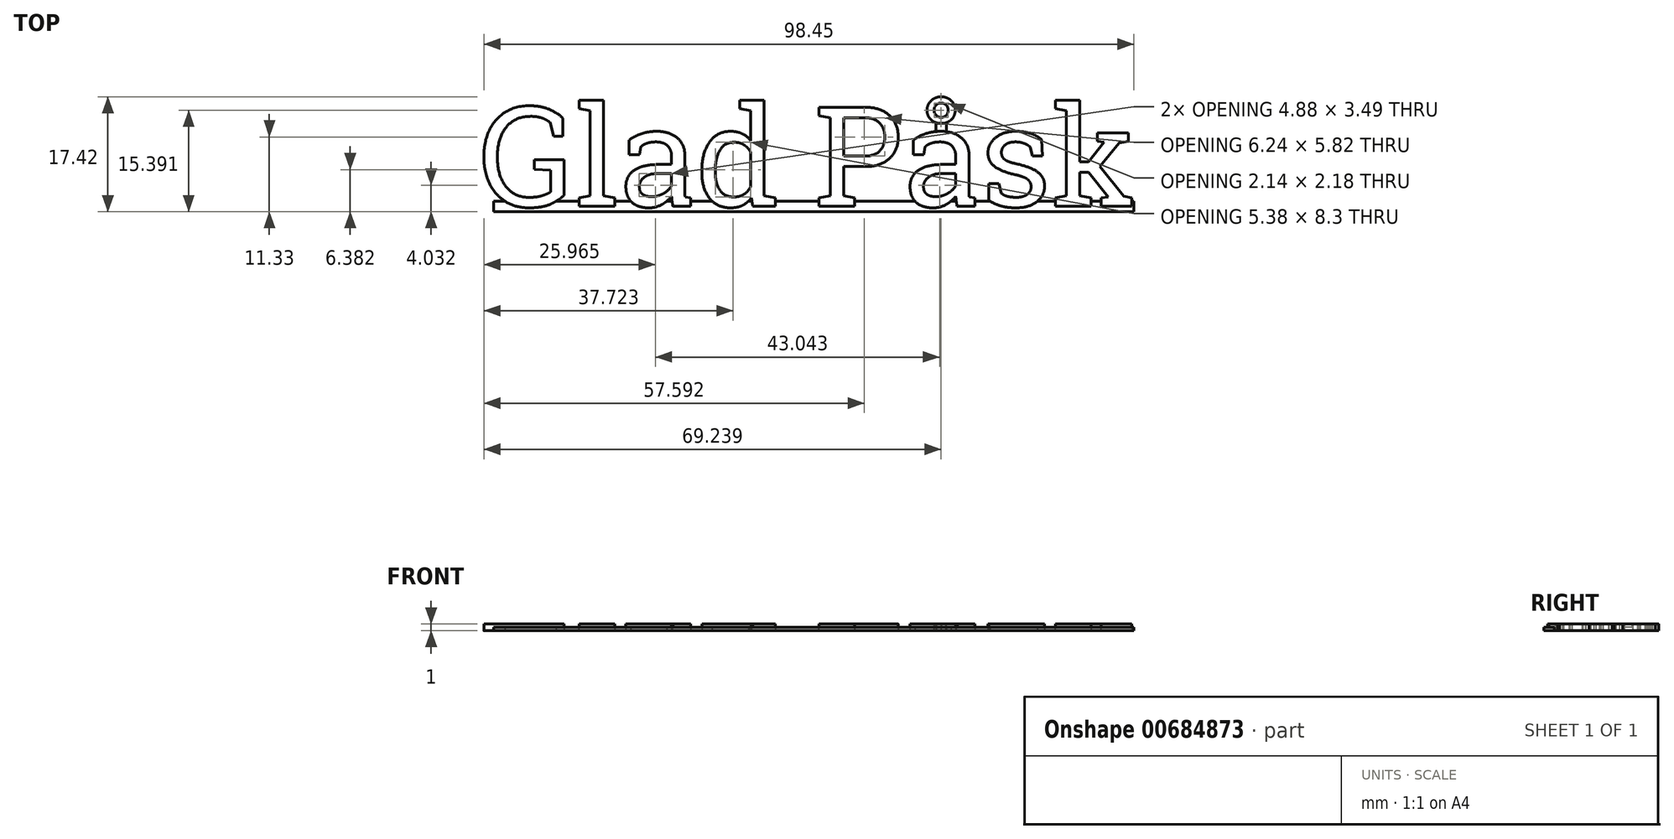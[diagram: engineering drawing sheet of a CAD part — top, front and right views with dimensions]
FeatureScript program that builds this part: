
annotation { "Feature Type Name" : "Feature", "Feature Type Description" : "" }
export const myFeature = defineFeature(function(context is Context, id is Id, definition is map)
    precondition{}
    {
        {
            var Q0;
            Q0=qCreatedBy(makeId("Top.planeOp"),FACE);
            var sketch = newSketch(context, id + "F0", { "sketchPlane" : qUnion([Q0])});
            skText(sketch, "E0", { "text": "Glad Påsk", "fontName": "RobotoSlab-Regular.ttf"});
            skLineSegment(sketch, "E1.bottom", {"start": v(-47.98, -0.8) * mm, "end": v(49.02, -0.8) * mm});
            skLineSegment(sketch, "E1.top", {"start": v(-47.98, 0.8) * mm, "end": v(49.02, 0.8) * mm});
            skLineSegment(sketch, "E1.left", {"start": v(-47.98, -0.8) * mm, "end": v(-47.98, 0.8) * mm});
            skLineSegment(sketch, "E1.right", {"start": v(49.02, -0.8) * mm, "end": v(49.02, 0.8) * mm});
            skLineSegment(sketch, "E2.bottom", {"start": v(19.01, 13.23) * mm, "end": v(20.61, 13.23) * mm});
            skLineSegment(sketch, "E2.top", {"start": v(19.01, 10.73) * mm, "end": v(20.61, 10.73) * mm});
            skLineSegment(sketch, "E2.left", {"start": v(19.01, 13.23) * mm, "end": v(19.01, 10.73) * mm});
            skLineSegment(sketch, "E2.right", {"start": v(20.61, 13.23) * mm, "end": v(20.61, 10.73) * mm});
            const initialGuessF0  = {"E0": [-0.05, 0, 1, 0, 0.01523]};
            skSetInitialGuess(sketch, initialGuessF0);
            skSolve(sketch);
        }
        {
            var Q0;
            {var subQ32=sQuery(id+"F0.wireOp",EDGE,"E0.sketch_text.stroke-1");Q0=makeQuery(id+"F0.imprint","IMPRINT",FACE,{"disambiguationData":[TD([[makeQuery(id+"F0.imprint","IMPRINT",EDGE,{"derivedFrom":subQ32}),1.0]])]});}
            var Q1;
            {var subQ0=sQuery(id+"F0.wireOp",EDGE,"E0.sketch_text.stroke-108");Q1=makeQuery(id+"F0.imprint","IMPRINT",FACE,{"disambiguationData":[TD([[makeQuery(id+"F0.imprint","IMPRINT",EDGE,{"derivedFrom":subQ0}),-1.0]])]});}
            var Q2;
            {var subQ0=sQuery(id+"F0.wireOp",EDGE,"E0.sketch_text.stroke-88");Q2=makeQuery(id+"F0.imprint","IMPRINT",FACE,{"disambiguationData":[TD([[makeQuery(id+"F0.imprint","IMPRINT",EDGE,{"derivedFrom":subQ0}),-1.0]])]});}
            var Q3;
            {var subQ0=sQuery(id+"F0.wireOp",EDGE,"E0.sketch_text.stroke-72");Q3=makeQuery(id+"F0.imprint","IMPRINT",FACE,{"disambiguationData":[TD([[makeQuery(id+"F0.imprint","IMPRINT",EDGE,{"derivedFrom":subQ0}),-1.0]])]});}
            var Q4;
            {var subQ0=sQuery(id+"F0.wireOp",EDGE,"E0.sketch_text.stroke-62");Q4=makeQuery(id+"F0.imprint","IMPRINT",FACE,{"disambiguationData":[TD([[makeQuery(id+"F0.imprint","IMPRINT",EDGE,{"derivedFrom":subQ0}),-1.0]])]});}
            var Q5;
            {var subQ4=sQuery(id+"F0.wireOp",EDGE,"E0.sketch_text.stroke-39");Q5=makeQuery(id+"F0.imprint","IMPRINT",FACE,{"disambiguationData":[TD([[makeQuery(id+"F0.imprint","IMPRINT",EDGE,{"derivedFrom":subQ4}),-1.0]])]});}
            var Q6;
            {var subQ0=sQuery(id+"F0.wireOp",EDGE,"E0.sketch_text.stroke-31");Q6=makeQuery(id+"F0.imprint","IMPRINT",FACE,{"disambiguationData":[TD([[makeQuery(id+"F0.imprint","IMPRINT",EDGE,{"derivedFrom":subQ0}),-1.0]])]});}
            var Q7;
            {var subQ0=sQuery(id+"F0.wireOp",EDGE,"E0.sketch_text.stroke-1");Q7=makeQuery(id+"F0.imprint","IMPRINT",FACE,{"disambiguationData":[TD([[makeQuery(id+"F0.imprint","IMPRINT",EDGE,{"derivedFrom":subQ0}),-1.0]])]});}
            var Q8;
            {var subQ6=sQuery(id+"F0.wireOp",EDGE,"E0.sketch_text.stroke-126");Q8=makeQuery(id+"F0.imprint","IMPRINT",FACE,{"disambiguationData":[TD([[makeQuery(id+"F0.imprint","IMPRINT",EDGE,{"derivedFrom":subQ6}),-1.0]])]});}
            var Q9;
            {var subQ0=sQuery(id+"F0.wireOp",EDGE,"E0.sketch_text.stroke-149");Q9=makeQuery(id+"F0.imprint","IMPRINT",FACE,{"disambiguationData":[TD([[makeQuery(id+"F0.imprint","IMPRINT",EDGE,{"derivedFrom":subQ0}),-1.0]])]});}
            var Q10;
            {var subQ4=sQuery(id+"F0.wireOp",EDGE,"E0.sketch_text.stroke-185");Q10=makeQuery(id+"F0.imprint","IMPRINT",FACE,{"disambiguationData":[TD([[makeQuery(id+"F0.imprint","IMPRINT",EDGE,{"derivedFrom":subQ4}),-1.0]])]});}
            var Q11;
            {var subQ0=sQuery(id+"F0.wireOp",EDGE,"E0.sketch_text.stroke-226");Q11=makeQuery(id+"F0.imprint","IMPRINT",FACE,{"disambiguationData":[TD([[makeQuery(id+"F0.imprint","IMPRINT",EDGE,{"derivedFrom":subQ0}),-1.0]])]});}
            var Q12;
            {var subQ0=sQuery(id+"F0.wireOp",EDGE,"E0.sketch_text.stroke-218");Q12=makeQuery(id+"F0.imprint","IMPRINT",FACE,{"disambiguationData":[TD([[makeQuery(id+"F0.imprint","IMPRINT",EDGE,{"derivedFrom":subQ0}),-1.0]])]});}
            var Q13;
            {var subQ0=sQuery(id+"F0.wireOp",EDGE,"E2.bottom");Q13=makeQuery(id+"F0.imprint","IMPRINT",FACE,{"disambiguationData":[TD([[makeQuery(id+"F0.imprint","IMPRINT",EDGE,{"derivedFrom":subQ0}),-1.0]])]});}
            var Q14;
            {var subQ5=sQuery(id+"F0.wireOp",EDGE,"E0.sketch_text.stroke-142");var subQ6=sQuery(id+"F0.wireOp",EDGE,"E0.sketch_text.stroke-141");var subQ7=makeQuery(id+"F0.imprint","INTERSECT",VERTEX,{"derivedFrom":[subQ6,subQ5]});Q14=makeQuery(id+"F0.imprint","IMPRINT",FACE,{"disambiguationData":[TD([[makeQuery(id+"F0.imprint","IMPRINT",EDGE,{"disambiguationData":[TD([[subQ7,1.0]])],"derivedFrom":subQ6}),1.0]])]});}
            var Q15;
            {var subQ1=sQuery(id+"F0.wireOp",EDGE,"E2.top");Q15=makeQuery(id+"F0.imprint","IMPRINT",FACE,{"disambiguationData":[TD([[makeQuery(id+"F0.imprint","IMPRINT",EDGE,{"derivedFrom":subQ1}),1.0]])]});}
            extrude(context, id + "F1", {"entities" : qUnion([Q0, Q1, Q2, Q3, Q4, Q5, Q6, Q7, Q8, Q9, Q10, Q11, Q12, Q13, Q14, Q15]), "depth" : 0.5 * mm, "offsetDistance" : 25 * mm});
        }
        {
            var Q0;
            Q0=makeQuery(id+"F0.imprint","IMPRINT",FACE,{"disambiguationData":[TD([[makeQuery(id+"F0.imprint","IMPRINT",EDGE,{"derivedFrom":sQuery(id+"F0.wireOp",EDGE,"E0.sketch_text.stroke-204")}),-1.0]])]});
            var Q1;
            Q1=makeQuery(id+"F0.imprint","IMPRINT",FACE,{"disambiguationData":[TD([[makeQuery(id+"F0.imprint","IMPRINT",EDGE,{"derivedFrom":sQuery(id+"F0.wireOp",EDGE,"E0.sketch_text.stroke-174")}),-1.0]])]});
            var Q2;
            {var subQ13=sQuery(id+"F0.wireOp",EDGE,"E0.sketch_text.stroke-124");Q2=makeQuery(id+"F0.imprint","IMPRINT",FACE,{"disambiguationData":[TD([[makeQuery(id+"F0.imprint","IMPRINT",EDGE,{"derivedFrom":subQ13}),-1.0]])]});}
            var Q3;
            Q3=makeQuery(id+"F0.imprint","IMPRINT",FACE,{"disambiguationData":[TD([[makeQuery(id+"F0.imprint","IMPRINT",EDGE,{"derivedFrom":sQuery(id+"F0.wireOp",EDGE,"E0.sketch_text.stroke-158")}),-1.0]])]});
            var Q4;
            {var subQ0=sQuery(id+"F0.wireOp",EDGE,"E2.bottom");Q4=makeQuery(id+"F0.imprint","IMPRINT",FACE,{"disambiguationData":[TD([[makeQuery(id+"F0.imprint","IMPRINT",EDGE,{"derivedFrom":subQ0}),-1.0]])]});}
            var Q5;
            {var subQ1=sQuery(id+"F0.wireOp",EDGE,"E2.top");Q5=makeQuery(id+"F0.imprint","IMPRINT",FACE,{"disambiguationData":[TD([[makeQuery(id+"F0.imprint","IMPRINT",EDGE,{"derivedFrom":subQ1}),1.0]])]});}
            var Q6;
            {var subQ0=sQuery(id+"F0.wireOp",EDGE,"E0.sketch_text.stroke-218");Q6=makeQuery(id+"F0.imprint","IMPRINT",FACE,{"disambiguationData":[TD([[makeQuery(id+"F0.imprint","IMPRINT",EDGE,{"derivedFrom":subQ0}),-1.0]])]});}
            var Q7;
            {var subQ0=sQuery(id+"F0.wireOp",EDGE,"E0.sketch_text.stroke-226");Q7=makeQuery(id+"F0.imprint","IMPRINT",FACE,{"disambiguationData":[TD([[makeQuery(id+"F0.imprint","IMPRINT",EDGE,{"derivedFrom":subQ0}),-1.0]])]});}
            var Q8;
            {var subQ4=sQuery(id+"F0.wireOp",EDGE,"E0.sketch_text.stroke-185");Q8=makeQuery(id+"F0.imprint","IMPRINT",FACE,{"disambiguationData":[TD([[makeQuery(id+"F0.imprint","IMPRINT",EDGE,{"derivedFrom":subQ4}),-1.0]])]});}
            var Q9;
            {var subQ0=sQuery(id+"F0.wireOp",EDGE,"E0.sketch_text.stroke-149");Q9=makeQuery(id+"F0.imprint","IMPRINT",FACE,{"disambiguationData":[TD([[makeQuery(id+"F0.imprint","IMPRINT",EDGE,{"derivedFrom":subQ0}),-1.0]])]});}
            var Q10;
            {var subQ6=sQuery(id+"F0.wireOp",EDGE,"E0.sketch_text.stroke-126");Q10=makeQuery(id+"F0.imprint","IMPRINT",FACE,{"disambiguationData":[TD([[makeQuery(id+"F0.imprint","IMPRINT",EDGE,{"derivedFrom":subQ6}),-1.0]])]});}
            var Q11;
            Q11=makeQuery(id+"F0.imprint","IMPRINT",FACE,{"disambiguationData":[TD([[makeQuery(id+"F0.imprint","IMPRINT",EDGE,{"derivedFrom":sQuery(id+"F0.wireOp",EDGE,"E0.sketch_text.stroke-100")}),-1.0]])]});
            var Q12;
            {var subQ0=sQuery(id+"F0.wireOp",EDGE,"E0.sketch_text.stroke-108");Q12=makeQuery(id+"F0.imprint","IMPRINT",FACE,{"disambiguationData":[TD([[makeQuery(id+"F0.imprint","IMPRINT",EDGE,{"derivedFrom":subQ0}),-1.0]])]});}
            var Q13;
            {var subQ0=sQuery(id+"F0.wireOp",EDGE,"E0.sketch_text.stroke-88");Q13=makeQuery(id+"F0.imprint","IMPRINT",FACE,{"disambiguationData":[TD([[makeQuery(id+"F0.imprint","IMPRINT",EDGE,{"derivedFrom":subQ0}),-1.0]])]});}
            var Q14;
            {var subQ8=sQuery(id+"F0.wireOp",EDGE,"E0.sketch_text.stroke-74");Q14=makeQuery(id+"F0.imprint","IMPRINT",FACE,{"disambiguationData":[TD([[makeQuery(id+"F0.imprint","IMPRINT",EDGE,{"derivedFrom":subQ8}),-1.0]])]});}
            var Q15;
            {var subQ0=sQuery(id+"F0.wireOp",EDGE,"E0.sketch_text.stroke-72");Q15=makeQuery(id+"F0.imprint","IMPRINT",FACE,{"disambiguationData":[TD([[makeQuery(id+"F0.imprint","IMPRINT",EDGE,{"derivedFrom":subQ0}),-1.0]])]});}
            var Q16;
            {var subQ5=sQuery(id+"F0.wireOp",EDGE,"E0.sketch_text.stroke-37");Q16=makeQuery(id+"F0.imprint","IMPRINT",FACE,{"disambiguationData":[TD([[makeQuery(id+"F0.imprint","IMPRINT",EDGE,{"derivedFrom":subQ5}),-1.0]])]});}
            var Q17;
            Q17=makeQuery(id+"F0.imprint","IMPRINT",FACE,{"disambiguationData":[TD([[makeQuery(id+"F0.imprint","IMPRINT",EDGE,{"derivedFrom":sQuery(id+"F0.wireOp",EDGE,"E0.sketch_text.stroke-26")}),-1.0]])]});
            var Q18;
            {var subQ0=sQuery(id+"F0.wireOp",EDGE,"E0.sketch_text.stroke-3");Q18=makeQuery(id+"F0.imprint","IMPRINT",FACE,{"disambiguationData":[TD([[makeQuery(id+"F0.imprint","IMPRINT",EDGE,{"derivedFrom":subQ0}),-1.0]])]});}
            var Q19;
            {var subQ0=sQuery(id+"F0.wireOp",EDGE,"E0.sketch_text.stroke-1");Q19=makeQuery(id+"F0.imprint","IMPRINT",FACE,{"disambiguationData":[TD([[makeQuery(id+"F0.imprint","IMPRINT",EDGE,{"derivedFrom":subQ0}),-1.0]])]});}
            var Q20;
            {var subQ0=sQuery(id+"F0.wireOp",EDGE,"E0.sketch_text.stroke-31");Q20=makeQuery(id+"F0.imprint","IMPRINT",FACE,{"disambiguationData":[TD([[makeQuery(id+"F0.imprint","IMPRINT",EDGE,{"derivedFrom":subQ0}),-1.0]])]});}
            var Q21;
            {var subQ4=sQuery(id+"F0.wireOp",EDGE,"E0.sketch_text.stroke-39");Q21=makeQuery(id+"F0.imprint","IMPRINT",FACE,{"disambiguationData":[TD([[makeQuery(id+"F0.imprint","IMPRINT",EDGE,{"derivedFrom":subQ4}),-1.0]])]});}
            var Q22;
            {var subQ0=sQuery(id+"F0.wireOp",EDGE,"E0.sketch_text.stroke-62");Q22=makeQuery(id+"F0.imprint","IMPRINT",FACE,{"disambiguationData":[TD([[makeQuery(id+"F0.imprint","IMPRINT",EDGE,{"derivedFrom":subQ0}),-1.0]])]});}
            extrude(context, id + "F2", {"entities" : qUnion([Q0, Q1, Q2, Q3, Q4, Q5, Q6, Q7, Q8, Q9, Q10, Q11, Q12, Q13, Q14, Q15, Q16, Q17, Q18, Q19, Q20, Q21, Q22]), "operationType" : NewBodyOperationType.ADD, "depth" : 1 * mm, "offsetDistance" : 25 * mm});
        }
    });
